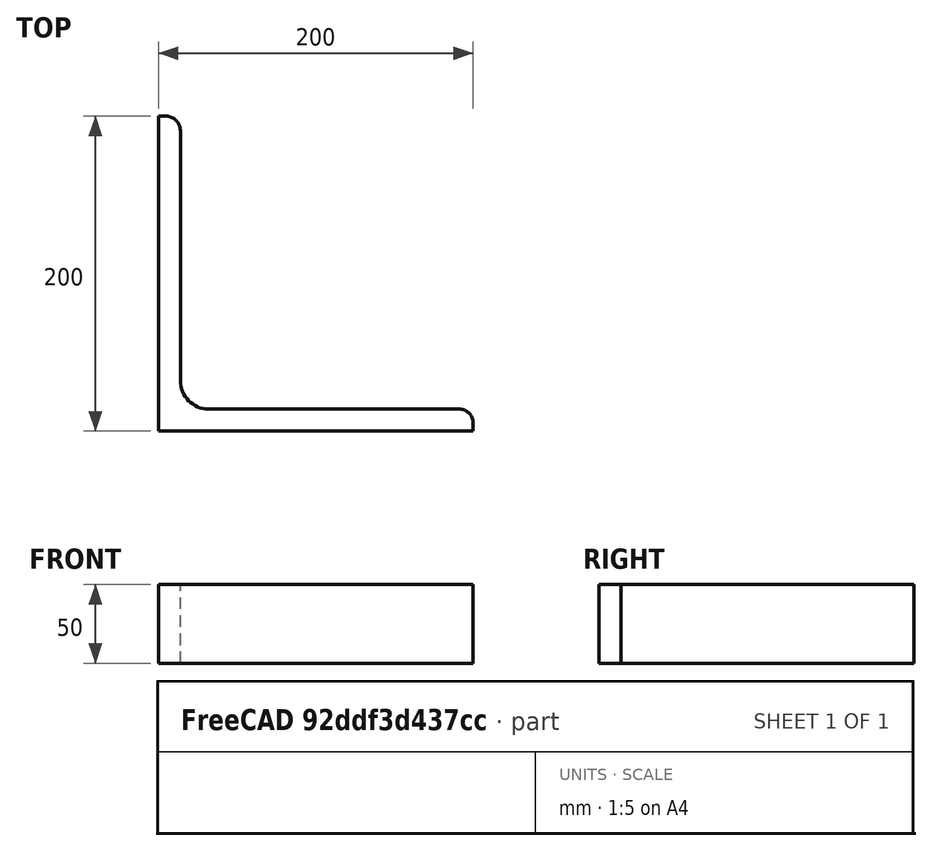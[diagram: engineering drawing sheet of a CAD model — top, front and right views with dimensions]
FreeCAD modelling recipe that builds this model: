
FCSTD DOCUMENT  (FreeCAD 0.15R4671 (Git))
Label: Angle Bar L200x200x14 EN10056 S235JR
License: All rights reserved
LicenseURL: http://en.wikipedia.org/wiki/All_rights_reserved
objects: Sketcher::SketchObject×1, Part::Extrusion×1
note: 2 computed .brp shape members not serialized (recipe doc carries the construction recipe); baked Part::Feature solids carry a one-line shape summary decoded from their .brp

FEATURE [Sketcher::SketchObject] Sketch
  sketch-geometry (9):
    g0: LineSegment StartX=0 StartY=0 StartZ=0 EndX=200 EndY=0 EndZ=0
    g1: LineSegment StartX=200 StartY=0 StartZ=0 EndX=200 EndY=5 EndZ=0
    g2: LineSegment StartX=191 StartY=14 StartZ=0 EndX=32 EndY=14 EndZ=0
    g3: LineSegment StartX=0 StartY=0 StartZ=0 EndX=0 EndY=200 EndZ=0
    g4: LineSegment StartX=0 StartY=200 StartZ=0 EndX=5 EndY=200 EndZ=0
    g5: LineSegment StartX=14 StartY=191 StartZ=0 EndX=14 EndY=32 EndZ=0
    g6: ArcOfCircle CenterX=32 CenterY=32 CenterZ=0 NormalX=0 NormalY=0 NormalZ=1 Radius=18 StartAngle=3.14159 EndAngle=4.71239
    g7: ArcOfCircle CenterX=5 CenterY=191 CenterZ=0 NormalX=0 NormalY=0 NormalZ=1 Radius=9 StartAngle=0 EndAngle=1.5708
    g8: ArcOfCircle CenterX=191 CenterY=5 CenterZ=0 NormalX=0 NormalY=0 NormalZ=1 Radius=9 StartAngle=0 EndAngle=1.5708
  constraints (23):
    c: Coincident(g0,g-1)
    c: Horizontal(g0)
    c: Coincident(g1,g0)
    c: Vertical(g1)
    c: Horizontal(g2)
    c: Coincident(g3,g-1)
    c: Vertical(g3)
    c: Coincident(g4,g3)
    c: Horizontal(g4)
    c: Vertical(g5)
    c: Tangent(g5,g6) = -1.5708
    c: Tangent(g2,g6) = 1.5708
    c: Tangent(g4,g7) = 1.5708
    c: Tangent(g5,g7) = 1.5708
    c: Tangent(g2,g8) = -1.5708
    c: Tangent(g1,g8) = -1.5708
    c: DistanceX(g0) = 200
    c: DistanceY(g3) = 200
    c: DistanceY(g0,g2) = 14
    c: DistanceX(g3,g5) = 14
    c: Radius(g6) = 18
    c: Radius(g8) = 9
    c: Radius(g7) = 9
FEATURE [Part::Extrusion] Extrude  label="Angle Bar L200x200x14 EN10056 S235JR"
  Base = -> Sketch
  Dir = (0,0,50)
  Solid = true
